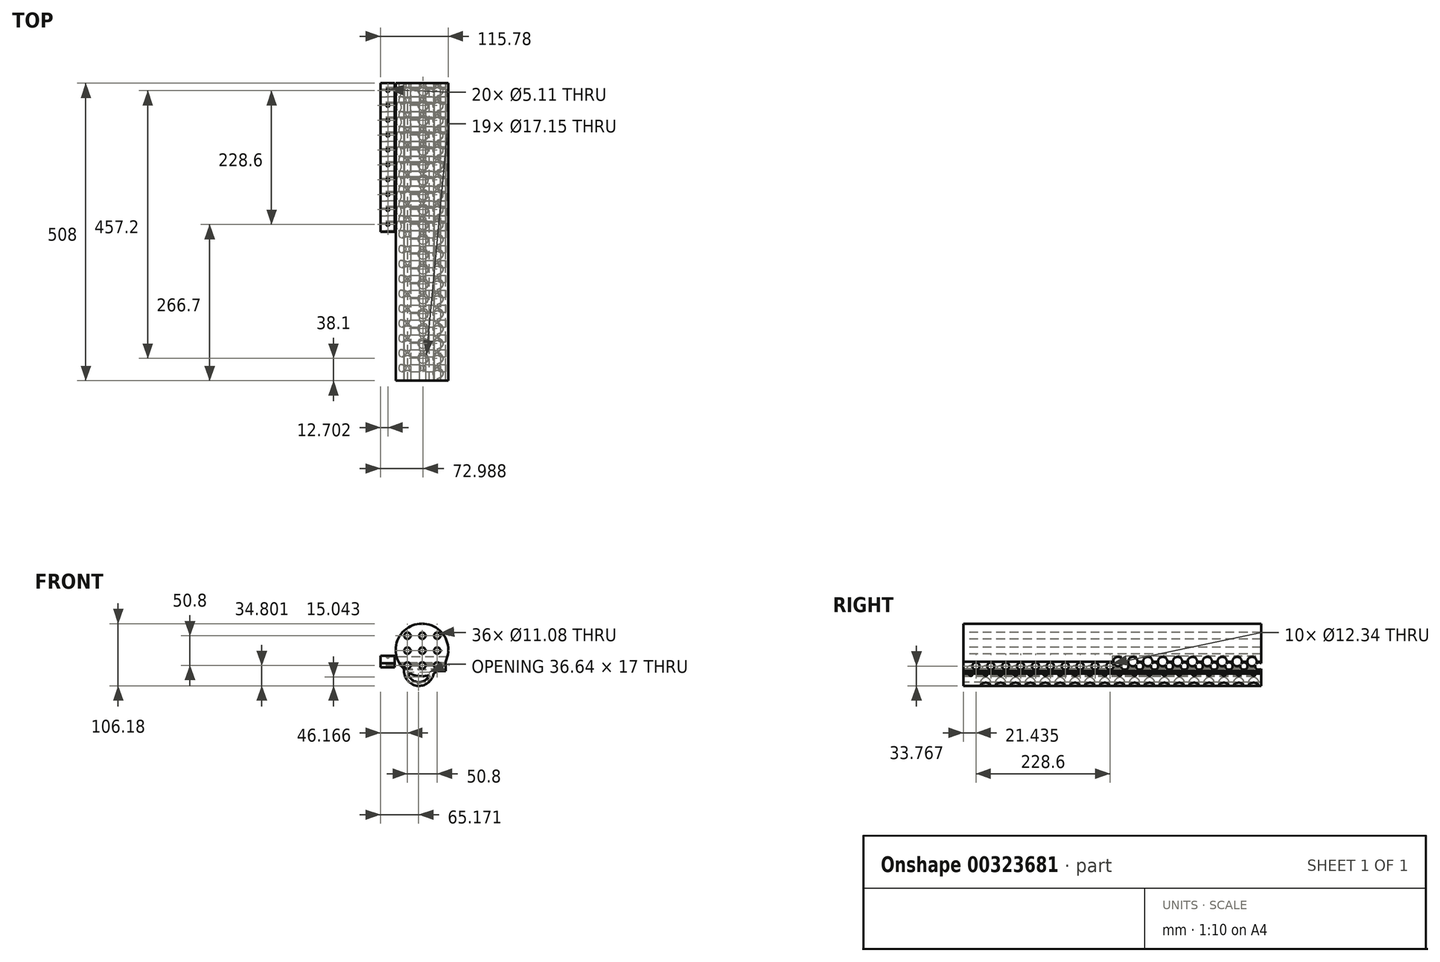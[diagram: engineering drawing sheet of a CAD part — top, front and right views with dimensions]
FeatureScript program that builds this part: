
annotation { "Feature Type Name" : "Feature", "Feature Type Description" : "" }
export const myFeature = defineFeature(function(context is Context, id is Id, definition is map)
    precondition{}
    {
        {
            var Q0;
            Q0=qCreatedBy(makeId("Front.planeOp"),FACE);
            var sketch = newSketch(context, id + "F0", { "sketchPlane" : qUnion([Q0])});
            skCircle(sketch, "E0", {"center": v(0, 0) * mm, "radius": 25.4 * mm});
            skSolve(sketch);
        }
        {
            var Q0;
            Q0=makeQuery(id+"F0.imprint","IMPRINT",FACE,{"disambiguationData":[TD([[makeQuery(id+"F0.imprint","IMPRINT",EDGE,{"derivedFrom":sQuery(id+"F0.wireOp",EDGE,"E0")}),1.0]])]});
            extrude(context, id + "F1", {"entities" : qUnion([Q0]), "depth" : 508 * mm});
        }
        {
            var Q0;
            Q0=makeQuery(id+"F1.opExtrude","CAP_FACE",FACE,{"disambiguationData":[OSD([sQuery(id+"F0.wireOp",EDGE,"E0")])],"isStart":false});
            var sketch = newSketch(context, id + "F2", { "sketchPlane" : qUnion([Q0])});
            skCircle(sketch, "E1", {"center": v(0, 0) * mm, "radius": 19.05 * mm});
            skSolve(sketch);
        }
        {
            var Q0;
            Q0=makeQuery(id+"F2.imprint","IMPRINT",FACE,{"disambiguationData":[TD([[makeQuery(id+"F2.imprint","IMPRINT",EDGE,{"derivedFrom":sQuery(id+"F2.wireOp",EDGE,"E1")}),1.0]])]});
            extrude(context, id + "F3", {"entities" : qUnion([Q0]), "operationType" : NewBodyOperationType.REMOVE, "oppositeDirection" : true, "depth" : 508 * mm});
        }
        {
            var Q0;
            Q0=qCreatedBy(makeId("Front.planeOp"),FACE);
            var sketch = newSketch(context, id + "F4", { "sketchPlane" : qUnion([Q0])});
            skLineSegment(sketch, "E2.bottom", {"start": v(-65.8, 26.01) * mm, "end": v(-41.62, 26.01) * mm});
            skLineSegment(sketch, "E2.top", {"start": v(-65.8, 6.33) * mm, "end": v(-41.62, 6.33) * mm});
            skLineSegment(sketch, "E2.left", {"start": v(-65.8, 26.01) * mm, "end": v(-65.8, 6.33) * mm});
            skLineSegment(sketch, "E2.right", {"start": v(-41.62, 26.01) * mm, "end": v(-41.62, 6.33) * mm});
            skSolve(sketch);
        }
        {
            var Q0;
            Q0=makeQuery(id+"F4.imprint","IMPRINT",FACE,{"disambiguationData":[TD([[makeQuery(id+"F4.imprint","IMPRINT",EDGE,{"derivedFrom":sQuery(id+"F4.wireOp",EDGE,"E2.bottom")}),-1.0]])]});
            extrude(context, id + "F5", {"entities" : qUnion([Q0]), "depth" : 254 * mm});
        }
        {
            var Q0;
            Q0=makeQuery(id+"F5.opExtrude","SWEPT_FACE",FACE,{"disambiguationData":[OSD([sQuery(id+"F4.wireOp",EDGE,"E2.top")])]});
            var sketch = newSketch(context, id + "F6", { "sketchPlane" : qUnion([Q0])});
            skCircle(sketch, "E3", {"center": v(-53.1, 241.3) * mm, "radius": 2.55 * mm});
            skCircle(sketch, "E4.0.1.0", {"center": v(-53.1, 215.9) * mm, "radius": 2.55 * mm});
            skCircle(sketch, "E4.0.2.0", {"center": v(-53.1, 190.5) * mm, "radius": 2.55 * mm});
            skCircle(sketch, "E4.0.3.0", {"center": v(-53.1, 165.1) * mm, "radius": 2.55 * mm});
            skCircle(sketch, "E4.0.4.0", {"center": v(-53.1, 139.7) * mm, "radius": 2.55 * mm});
            skCircle(sketch, "E4.0.5.0", {"center": v(-53.1, 114.3) * mm, "radius": 2.55 * mm});
            skCircle(sketch, "E4.0.6.0", {"center": v(-53.1, 88.9) * mm, "radius": 2.55 * mm});
            skCircle(sketch, "E4.0.7.0", {"center": v(-53.1, 63.5) * mm, "radius": 2.55 * mm});
            skCircle(sketch, "E4.0.8.0", {"center": v(-53.1, 38.1) * mm, "radius": 2.55 * mm});
            skCircle(sketch, "E4.0.9.0", {"center": v(-53.1, 12.7) * mm, "radius": 2.55 * mm});
            skLineSegment(sketch, "E4.direction1", {"start": v(-53.1, 241.3) * mm, "end": v(-27.7, 241.3) * mm, "construction": true});
            skLineSegment(sketch, "E4.direction2", {"start": v(-53.1, 241.3) * mm, "end": v(-53.1, 215.9) * mm, "construction": true});
            skSolve(sketch);
        }
        {
            var Q0;
            Q0 = qSketchRegion(id + "F6", true);
            extrude(context, id + "F7", {"entities" : qUnion([Q0]), "operationType" : NewBodyOperationType.REMOVE, "oppositeDirection" : true, "depth" : 254 * mm});
        }
        {
            var Q0;
            Q0=qCreatedBy(makeId("Front.planeOp"),FACE);
            var sketch = newSketch(context, id + "F8", { "sketchPlane" : qUnion([Q0])});
            skLineSegment(sketch, "E5.bottom", {"start": v(-16.31, 30.8) * mm, "end": v(45.28, 30.8) * mm});
            skLineSegment(sketch, "E5.top", {"start": v(-16.31, 0) * mm, "end": v(45.28, 0) * mm});
            skLineSegment(sketch, "E5.left", {"start": v(-16.31, 30.8) * mm, "end": v(-16.31, 0) * mm});
            skLineSegment(sketch, "E5.right", {"start": v(45.28, 30.8) * mm, "end": v(45.28, 0) * mm});
            skSolve(sketch);
        }
        {
            var Q0;
            Q0=makeQuery(id+"F8.imprint","IMPRINT",FACE,{"disambiguationData":[TD([[makeQuery(id+"F8.imprint","IMPRINT",EDGE,{"derivedFrom":sQuery(id+"F8.wireOp",EDGE,"E5.bottom")}),-1.0]])]});
            extrude(context, id + "F9", {"entities" : qUnion([Q0]), "operationType" : NewBodyOperationType.ADD, "depth" : 508 * mm});
        }
        {
            var Q0;
            Q0=makeQuery(id+"F9.opExtrude","SWEPT_FACE",FACE,{"disambiguationData":[OSD([sQuery(id+"F8.wireOp",EDGE,"E5.bottom")])]});
            var sketch = newSketch(context, id + "F10", { "sketchPlane" : qUnion([Q0])});
            skCircle(sketch, "E6", {"center": v(32.58, -495.3) * mm, "radius": 8.58 * mm});
            skCircle(sketch, "E7.0.1.0", {"center": v(32.58, -469.9) * mm, "radius": 8.58 * mm});
            skCircle(sketch, "E7.0.2.0", {"center": v(32.58, -444.5) * mm, "radius": 8.58 * mm});
            skCircle(sketch, "E7.0.3.0", {"center": v(32.58, -419.1) * mm, "radius": 8.58 * mm});
            skCircle(sketch, "E7.0.4.0", {"center": v(32.58, -393.7) * mm, "radius": 8.58 * mm});
            skCircle(sketch, "E7.0.5.0", {"center": v(32.58, -368.3) * mm, "radius": 8.58 * mm});
            skCircle(sketch, "E7.0.6.0", {"center": v(32.58, -342.9) * mm, "radius": 8.58 * mm});
            skCircle(sketch, "E7.0.7.0", {"center": v(32.58, -317.5) * mm, "radius": 8.58 * mm});
            skCircle(sketch, "E7.0.8.0", {"center": v(32.58, -292.1) * mm, "radius": 8.58 * mm});
            skCircle(sketch, "E7.0.9.0", {"center": v(32.58, -266.7) * mm, "radius": 8.58 * mm});
            skCircle(sketch, "E7.0.10.0", {"center": v(32.58, -241.3) * mm, "radius": 8.58 * mm});
            skCircle(sketch, "E7.0.11.0", {"center": v(32.58, -215.9) * mm, "radius": 8.58 * mm});
            skCircle(sketch, "E7.0.12.0", {"center": v(32.58, -190.5) * mm, "radius": 8.58 * mm});
            skCircle(sketch, "E7.0.13.0", {"center": v(32.58, -165.1) * mm, "radius": 8.58 * mm});
            skCircle(sketch, "E7.0.14.0", {"center": v(32.58, -139.7) * mm, "radius": 8.58 * mm});
            skCircle(sketch, "E7.0.15.0", {"center": v(32.58, -114.3) * mm, "radius": 8.58 * mm});
            skCircle(sketch, "E7.0.16.0", {"center": v(32.58, -88.9) * mm, "radius": 8.58 * mm});
            skCircle(sketch, "E7.0.17.0", {"center": v(32.58, -63.5) * mm, "radius": 8.58 * mm});
            skCircle(sketch, "E7.0.18.0", {"center": v(32.58, -38.1) * mm, "radius": 8.58 * mm});
            skCircle(sketch, "E7.0.19.0", {"center": v(32.58, -12.7) * mm, "radius": 8.58 * mm});
            skCircle(sketch, "E7.1.0.0", {"center": v(7.18, -495.3) * mm, "radius": 8.58 * mm});
            skCircle(sketch, "E7.1.1.0", {"center": v(7.18, -469.9) * mm, "radius": 8.58 * mm});
            skCircle(sketch, "E7.1.2.0", {"center": v(7.18, -444.5) * mm, "radius": 8.58 * mm});
            skCircle(sketch, "E7.1.3.0", {"center": v(7.18, -419.1) * mm, "radius": 8.58 * mm});
            skCircle(sketch, "E7.1.4.0", {"center": v(7.18, -393.7) * mm, "radius": 8.58 * mm});
            skCircle(sketch, "E7.1.5.0", {"center": v(7.18, -368.3) * mm, "radius": 8.58 * mm});
            skCircle(sketch, "E7.1.6.0", {"center": v(7.18, -342.9) * mm, "radius": 8.58 * mm});
            skCircle(sketch, "E7.1.7.0", {"center": v(7.18, -317.5) * mm, "radius": 8.58 * mm});
            skCircle(sketch, "E7.1.8.0", {"center": v(7.18, -292.1) * mm, "radius": 8.58 * mm});
            skCircle(sketch, "E7.1.9.0", {"center": v(7.18, -266.7) * mm, "radius": 8.58 * mm});
            skCircle(sketch, "E7.1.10.0", {"center": v(7.18, -241.3) * mm, "radius": 8.58 * mm});
            skCircle(sketch, "E7.1.11.0", {"center": v(7.18, -215.9) * mm, "radius": 8.58 * mm});
            skCircle(sketch, "E7.1.12.0", {"center": v(7.18, -190.5) * mm, "radius": 8.58 * mm});
            skCircle(sketch, "E7.1.13.0", {"center": v(7.18, -165.1) * mm, "radius": 8.58 * mm});
            skCircle(sketch, "E7.1.14.0", {"center": v(7.18, -139.7) * mm, "radius": 8.58 * mm});
            skCircle(sketch, "E7.1.15.0", {"center": v(7.18, -114.3) * mm, "radius": 8.58 * mm});
            skCircle(sketch, "E7.1.16.0", {"center": v(7.18, -88.9) * mm, "radius": 8.58 * mm});
            skCircle(sketch, "E7.1.17.0", {"center": v(7.18, -63.5) * mm, "radius": 8.58 * mm});
            skCircle(sketch, "E7.1.18.0", {"center": v(7.18, -38.1) * mm, "radius": 8.58 * mm});
            skCircle(sketch, "E7.1.19.0", {"center": v(7.18, -12.7) * mm, "radius": 8.58 * mm});
            skLineSegment(sketch, "E7.direction1", {"start": v(32.58, -495.3) * mm, "end": v(7.18, -495.3) * mm, "construction": true});
            skLineSegment(sketch, "E7.direction2", {"start": v(32.58, -495.3) * mm, "end": v(32.58, -469.9) * mm, "construction": true});
            skSolve(sketch);
        }
        {
            var Q0;
            Q0=makeQuery(id+"F10.imprint","IMPRINT",FACE,{"disambiguationData":[TD([[makeQuery(id+"F10.imprint","IMPRINT",EDGE,{"derivedFrom":sQuery(id+"F10.wireOp",EDGE,"E6")}),1.0]])]});
            var Q1;
            Q1=makeQuery(id+"F10.imprint","IMPRINT",FACE,{"disambiguationData":[TD([[makeQuery(id+"F10.imprint","IMPRINT",EDGE,{"derivedFrom":sQuery(id+"F10.wireOp",EDGE,"E7.0.1.0")}),1.0]])]});
            var Q2;
            Q2=makeQuery(id+"F10.imprint","IMPRINT",FACE,{"disambiguationData":[TD([[makeQuery(id+"F10.imprint","IMPRINT",EDGE,{"derivedFrom":sQuery(id+"F10.wireOp",EDGE,"E7.0.2.0")}),1.0]])]});
            var Q3;
            Q3=makeQuery(id+"F10.imprint","IMPRINT",FACE,{"disambiguationData":[TD([[makeQuery(id+"F10.imprint","IMPRINT",EDGE,{"derivedFrom":sQuery(id+"F10.wireOp",EDGE,"E7.0.3.0")}),1.0]])]});
            var Q4;
            Q4=makeQuery(id+"F10.imprint","IMPRINT",FACE,{"disambiguationData":[TD([[makeQuery(id+"F10.imprint","IMPRINT",EDGE,{"derivedFrom":sQuery(id+"F10.wireOp",EDGE,"E7.0.4.0")}),1.0]])]});
            var Q5;
            Q5=makeQuery(id+"F10.imprint","IMPRINT",FACE,{"disambiguationData":[TD([[makeQuery(id+"F10.imprint","IMPRINT",EDGE,{"derivedFrom":sQuery(id+"F10.wireOp",EDGE,"E7.0.5.0")}),1.0]])]});
            var Q6;
            Q6=makeQuery(id+"F10.imprint","IMPRINT",FACE,{"disambiguationData":[TD([[makeQuery(id+"F10.imprint","IMPRINT",EDGE,{"derivedFrom":sQuery(id+"F10.wireOp",EDGE,"E7.0.6.0")}),1.0]])]});
            var Q7;
            Q7=makeQuery(id+"F10.imprint","IMPRINT",FACE,{"disambiguationData":[TD([[makeQuery(id+"F10.imprint","IMPRINT",EDGE,{"derivedFrom":sQuery(id+"F10.wireOp",EDGE,"E7.0.7.0")}),1.0]])]});
            var Q8;
            Q8=makeQuery(id+"F10.imprint","IMPRINT",FACE,{"disambiguationData":[TD([[makeQuery(id+"F10.imprint","IMPRINT",EDGE,{"derivedFrom":sQuery(id+"F10.wireOp",EDGE,"E7.0.8.0")}),1.0]])]});
            var Q9;
            Q9=makeQuery(id+"F10.imprint","IMPRINT",FACE,{"disambiguationData":[TD([[makeQuery(id+"F10.imprint","IMPRINT",EDGE,{"derivedFrom":sQuery(id+"F10.wireOp",EDGE,"E7.0.9.0")}),1.0]])]});
            var Q10;
            Q10=makeQuery(id+"F10.imprint","IMPRINT",FACE,{"disambiguationData":[TD([[makeQuery(id+"F10.imprint","IMPRINT",EDGE,{"derivedFrom":sQuery(id+"F10.wireOp",EDGE,"E7.0.10.0")}),1.0]])]});
            var Q11;
            Q11=makeQuery(id+"F10.imprint","IMPRINT",FACE,{"disambiguationData":[TD([[makeQuery(id+"F10.imprint","IMPRINT",EDGE,{"derivedFrom":sQuery(id+"F10.wireOp",EDGE,"E7.0.11.0")}),1.0]])]});
            var Q12;
            Q12=makeQuery(id+"F10.imprint","IMPRINT",FACE,{"disambiguationData":[TD([[makeQuery(id+"F10.imprint","IMPRINT",EDGE,{"derivedFrom":sQuery(id+"F10.wireOp",EDGE,"E7.0.12.0")}),1.0]])]});
            var Q13;
            Q13=makeQuery(id+"F10.imprint","IMPRINT",FACE,{"disambiguationData":[TD([[makeQuery(id+"F10.imprint","IMPRINT",EDGE,{"derivedFrom":sQuery(id+"F10.wireOp",EDGE,"E7.0.13.0")}),1.0]])]});
            var Q14;
            Q14=makeQuery(id+"F10.imprint","IMPRINT",FACE,{"disambiguationData":[TD([[makeQuery(id+"F10.imprint","IMPRINT",EDGE,{"derivedFrom":sQuery(id+"F10.wireOp",EDGE,"E7.0.14.0")}),1.0]])]});
            var Q15;
            Q15=makeQuery(id+"F10.imprint","IMPRINT",FACE,{"disambiguationData":[TD([[makeQuery(id+"F10.imprint","IMPRINT",EDGE,{"derivedFrom":sQuery(id+"F10.wireOp",EDGE,"E7.0.15.0")}),1.0]])]});
            var Q16;
            Q16=makeQuery(id+"F10.imprint","IMPRINT",FACE,{"disambiguationData":[TD([[makeQuery(id+"F10.imprint","IMPRINT",EDGE,{"derivedFrom":sQuery(id+"F10.wireOp",EDGE,"E7.0.16.0")}),1.0]])]});
            var Q17;
            Q17=makeQuery(id+"F10.imprint","IMPRINT",FACE,{"disambiguationData":[TD([[makeQuery(id+"F10.imprint","IMPRINT",EDGE,{"derivedFrom":sQuery(id+"F10.wireOp",EDGE,"E7.0.17.0")}),1.0]])]});
            var Q18;
            Q18=makeQuery(id+"F10.imprint","IMPRINT",FACE,{"disambiguationData":[TD([[makeQuery(id+"F10.imprint","IMPRINT",EDGE,{"derivedFrom":sQuery(id+"F10.wireOp",EDGE,"E7.0.18.0")}),1.0]])]});
            var Q19;
            Q19=makeQuery(id+"F10.imprint","IMPRINT",FACE,{"disambiguationData":[TD([[makeQuery(id+"F10.imprint","IMPRINT",EDGE,{"derivedFrom":sQuery(id+"F10.wireOp",EDGE,"E7.0.19.0")}),1.0]])]});
            var Q20;
            Q20=makeQuery(id+"F10.imprint","IMPRINT",FACE,{"disambiguationData":[TD([[makeQuery(id+"F10.imprint","IMPRINT",EDGE,{"derivedFrom":sQuery(id+"F10.wireOp",EDGE,"E7.1.1.0")}),1.0]])]});
            var Q21;
            Q21=makeQuery(id+"F10.imprint","IMPRINT",FACE,{"disambiguationData":[TD([[makeQuery(id+"F10.imprint","IMPRINT",EDGE,{"derivedFrom":sQuery(id+"F10.wireOp",EDGE,"E7.1.2.0")}),1.0]])]});
            var Q22;
            Q22=makeQuery(id+"F10.imprint","IMPRINT",FACE,{"disambiguationData":[TD([[makeQuery(id+"F10.imprint","IMPRINT",EDGE,{"derivedFrom":sQuery(id+"F10.wireOp",EDGE,"E7.1.3.0")}),1.0]])]});
            var Q23;
            Q23=makeQuery(id+"F10.imprint","IMPRINT",FACE,{"disambiguationData":[TD([[makeQuery(id+"F10.imprint","IMPRINT",EDGE,{"derivedFrom":sQuery(id+"F10.wireOp",EDGE,"E7.1.4.0")}),1.0]])]});
            var Q24;
            Q24=makeQuery(id+"F10.imprint","IMPRINT",FACE,{"disambiguationData":[TD([[makeQuery(id+"F10.imprint","IMPRINT",EDGE,{"derivedFrom":sQuery(id+"F10.wireOp",EDGE,"E7.1.5.0")}),1.0]])]});
            var Q25;
            Q25=makeQuery(id+"F10.imprint","IMPRINT",FACE,{"disambiguationData":[TD([[makeQuery(id+"F10.imprint","IMPRINT",EDGE,{"derivedFrom":sQuery(id+"F10.wireOp",EDGE,"E7.1.6.0")}),1.0]])]});
            var Q26;
            Q26=makeQuery(id+"F10.imprint","IMPRINT",FACE,{"disambiguationData":[TD([[makeQuery(id+"F10.imprint","IMPRINT",EDGE,{"derivedFrom":sQuery(id+"F10.wireOp",EDGE,"E7.1.7.0")}),1.0]])]});
            var Q27;
            Q27=makeQuery(id+"F10.imprint","IMPRINT",FACE,{"disambiguationData":[TD([[makeQuery(id+"F10.imprint","IMPRINT",EDGE,{"derivedFrom":sQuery(id+"F10.wireOp",EDGE,"E7.1.8.0")}),1.0]])]});
            var Q28;
            Q28=makeQuery(id+"F10.imprint","IMPRINT",FACE,{"disambiguationData":[TD([[makeQuery(id+"F10.imprint","IMPRINT",EDGE,{"derivedFrom":sQuery(id+"F10.wireOp",EDGE,"E7.1.9.0")}),1.0]])]});
            var Q29;
            Q29=makeQuery(id+"F10.imprint","IMPRINT",FACE,{"disambiguationData":[TD([[makeQuery(id+"F10.imprint","IMPRINT",EDGE,{"derivedFrom":sQuery(id+"F10.wireOp",EDGE,"E7.1.10.0")}),1.0]])]});
            var Q30;
            Q30=makeQuery(id+"F10.imprint","IMPRINT",FACE,{"disambiguationData":[TD([[makeQuery(id+"F10.imprint","IMPRINT",EDGE,{"derivedFrom":sQuery(id+"F10.wireOp",EDGE,"E7.1.11.0")}),1.0]])]});
            var Q31;
            Q31=makeQuery(id+"F10.imprint","IMPRINT",FACE,{"disambiguationData":[TD([[makeQuery(id+"F10.imprint","IMPRINT",EDGE,{"derivedFrom":sQuery(id+"F10.wireOp",EDGE,"E7.1.12.0")}),1.0]])]});
            var Q32;
            Q32=makeQuery(id+"F10.imprint","IMPRINT",FACE,{"disambiguationData":[TD([[makeQuery(id+"F10.imprint","IMPRINT",EDGE,{"derivedFrom":sQuery(id+"F10.wireOp",EDGE,"E7.1.13.0")}),1.0]])]});
            var Q33;
            Q33=makeQuery(id+"F10.imprint","IMPRINT",FACE,{"disambiguationData":[TD([[makeQuery(id+"F10.imprint","IMPRINT",EDGE,{"derivedFrom":sQuery(id+"F10.wireOp",EDGE,"E7.1.14.0")}),1.0]])]});
            var Q34;
            Q34=makeQuery(id+"F10.imprint","IMPRINT",FACE,{"disambiguationData":[TD([[makeQuery(id+"F10.imprint","IMPRINT",EDGE,{"derivedFrom":sQuery(id+"F10.wireOp",EDGE,"E7.1.15.0")}),1.0]])]});
            var Q35;
            Q35=makeQuery(id+"F10.imprint","IMPRINT",FACE,{"disambiguationData":[TD([[makeQuery(id+"F10.imprint","IMPRINT",EDGE,{"derivedFrom":sQuery(id+"F10.wireOp",EDGE,"E7.1.16.0")}),1.0]])]});
            var Q36;
            Q36=makeQuery(id+"F10.imprint","IMPRINT",FACE,{"disambiguationData":[TD([[makeQuery(id+"F10.imprint","IMPRINT",EDGE,{"derivedFrom":sQuery(id+"F10.wireOp",EDGE,"E7.1.17.0")}),1.0]])]});
            var Q37;
            Q37=makeQuery(id+"F10.imprint","IMPRINT",FACE,{"disambiguationData":[TD([[makeQuery(id+"F10.imprint","IMPRINT",EDGE,{"derivedFrom":sQuery(id+"F10.wireOp",EDGE,"E7.1.18.0")}),1.0]])]});
            var Q38;
            Q38=makeQuery(id+"F10.imprint","IMPRINT",FACE,{"disambiguationData":[TD([[makeQuery(id+"F10.imprint","IMPRINT",EDGE,{"derivedFrom":sQuery(id+"F10.wireOp",EDGE,"E7.1.19.0")}),1.0]])]});
            extrude(context, id + "F11", {"entities" : qUnion([Q0, Q1, Q2, Q3, Q4, Q5, Q6, Q7, Q8, Q9, Q10, Q11, Q12, Q13, Q14, Q15, Q16, Q17, Q18, Q19, Q20, Q21, Q22, Q23, Q24, Q25, Q26, Q27, Q28, Q29, Q30, Q31, Q32, Q33, Q34, Q35, Q36, Q37, Q38]), "operationType" : NewBodyOperationType.REMOVE, "oppositeDirection" : true, "depth" : 508 * mm});
        }
        {
            var Q0;
            Q0=qCreatedBy(makeId("Front.planeOp"),FACE);
            var sketch = newSketch(context, id + "F12", { "sketchPlane" : qUnion([Q0])});
            skCircle(sketch, "E8", {"center": v(5.14, 35.95) * mm, "radius": 44.83 * mm});
            skSolve(sketch);
        }
        {
            var Q0;
            Q0=makeQuery(id+"F12.imprint","IMPRINT",FACE,{"disambiguationData":[TD([[makeQuery(id+"F12.imprint","IMPRINT",EDGE,{"derivedFrom":sQuery(id+"F12.wireOp",EDGE,"E8")}),1.0]])]});
            extrude(context, id + "F13", {"entities" : qUnion([Q0]), "operationType" : NewBodyOperationType.ADD, "depth" : 508 * mm});
        }
        {
            var Q0;
            Q0=makeQuery(id+"F13.boolean.opBoolean","MERGE",FACE,{"derivedFrom":[makeQuery(id+"F9.boolean.opBoolean","MERGE",FACE,{"derivedFrom":[makeQuery(id+"F1.opExtrude","CAP_FACE",FACE,{"disambiguationData":[OSD([sQuery(id+"F0.wireOp",EDGE,"E0")])],"isStart":false}),makeQuery(id+"F9.opExtrude","CAP_FACE",FACE,{"disambiguationData":[OSD([sQuery(id+"F8.wireOp",EDGE,"E5.bottom"),sQuery(id+"F8.wireOp",EDGE,"E5.top"),sQuery(id+"F8.wireOp",EDGE,"E5.left"),sQuery(id+"F8.wireOp",EDGE,"E5.right")])],"isStart":false})]}),makeQuery(id+"F13.opExtrude","CAP_FACE",FACE,{"disambiguationData":[OSD([sQuery(id+"F12.wireOp",EDGE,"E8")])],"isStart":false})]});
            var sketch = newSketch(context, id + "F14", { "sketchPlane" : qUnion([Q0])});
            skCircle(sketch, "E9", {"center": v(-19.64, 60.2) * mm, "radius": 5.54 * mm});
            skCircle(sketch, "E10.0.1.0", {"center": v(-19.64, 34.8) * mm, "radius": 5.54 * mm});
            skCircle(sketch, "E10.0.2.0", {"center": v(-19.64, 9.4) * mm, "radius": 5.54 * mm});
            skCircle(sketch, "E10.1.0.0", {"center": v(5.76, 60.2) * mm, "radius": 5.54 * mm});
            skCircle(sketch, "E10.1.1.0", {"center": v(5.76, 34.8) * mm, "radius": 5.54 * mm});
            skCircle(sketch, "E10.1.2.0", {"center": v(5.76, 9.4) * mm, "radius": 5.54 * mm});
            skCircle(sketch, "E10.2.0.0", {"center": v(31.16, 60.2) * mm, "radius": 5.54 * mm});
            skCircle(sketch, "E10.2.1.0", {"center": v(31.16, 34.8) * mm, "radius": 5.54 * mm});
            skCircle(sketch, "E10.2.2.0", {"center": v(31.16, 9.4) * mm, "radius": 5.54 * mm});
            skLineSegment(sketch, "E10.direction1", {"start": v(-19.64, 60.2) * mm, "end": v(5.76, 60.2) * mm, "construction": true});
            skLineSegment(sketch, "E10.direction2", {"start": v(-19.64, 60.2) * mm, "end": v(-19.64, 34.8) * mm, "construction": true});
            skSolve(sketch);
        }
        {
            var Q0;
            Q0 = qSketchRegion(id + "F14", true);
            extrude(context, id + "F15", {"entities" : qUnion([Q0]), "operationType" : NewBodyOperationType.REMOVE, "oppositeDirection" : true, "depth" : 762 * mm});
        }
        {
            var Q0;
            Q0=makeQuery(id+"F9.opExtrude","SWEPT_FACE",FACE,{"disambiguationData":[OSD([sQuery(id+"F8.wireOp",EDGE,"E5.right")])]});
            var sketch = newSketch(context, id + "F16", { "sketchPlane" : qUnion([Q0])});
            skCircle(sketch, "E11", {"center": v(-486.57, 8.37) * mm, "radius": 6.17 * mm});
            skCircle(sketch, "E12.1.0.0", {"center": v(-461.17, 8.37) * mm, "radius": 6.17 * mm});
            skCircle(sketch, "E12.2.0.0", {"center": v(-435.77, 8.37) * mm, "radius": 6.17 * mm});
            skCircle(sketch, "E12.3.0.0", {"center": v(-410.37, 8.37) * mm, "radius": 6.17 * mm});
            skCircle(sketch, "E12.4.0.0", {"center": v(-384.97, 8.37) * mm, "radius": 6.17 * mm});
            skCircle(sketch, "E12.5.0.0", {"center": v(-359.57, 8.37) * mm, "radius": 6.17 * mm});
            skCircle(sketch, "E12.6.0.0", {"center": v(-334.17, 8.37) * mm, "radius": 6.17 * mm});
            skCircle(sketch, "E12.7.0.0", {"center": v(-308.77, 8.37) * mm, "radius": 6.17 * mm});
            skCircle(sketch, "E12.8.0.0", {"center": v(-283.37, 8.37) * mm, "radius": 6.17 * mm});
            skCircle(sketch, "E12.9.0.0", {"center": v(-257.97, 8.37) * mm, "radius": 6.17 * mm});
            skCircle(sketch, "E12.10.0.0", {"center": v(-232.57, 8.37) * mm, "radius": 6.17 * mm});
            skCircle(sketch, "E12.11.0.0", {"center": v(-207.17, 8.37) * mm, "radius": 6.17 * mm});
            skCircle(sketch, "E12.12.0.0", {"center": v(-181.77, 8.37) * mm, "radius": 6.17 * mm});
            skCircle(sketch, "E12.13.0.0", {"center": v(-156.37, 8.37) * mm, "radius": 6.17 * mm});
            skCircle(sketch, "E12.14.0.0", {"center": v(-130.97, 8.37) * mm, "radius": 6.17 * mm});
            skCircle(sketch, "E12.15.0.0", {"center": v(-105.57, 8.37) * mm, "radius": 6.17 * mm});
            skCircle(sketch, "E12.16.0.0", {"center": v(-80.17, 8.37) * mm, "radius": 6.17 * mm});
            skCircle(sketch, "E12.17.0.0", {"center": v(-54.77, 8.37) * mm, "radius": 6.17 * mm});
            skCircle(sketch, "E12.18.0.0", {"center": v(-29.37, 8.37) * mm, "radius": 6.17 * mm});
            skCircle(sketch, "E12.19.0.0", {"center": v(-3.97, 8.37) * mm, "radius": 6.17 * mm});
            skLineSegment(sketch, "E12.direction1", {"start": v(-486.57, 8.37) * mm, "end": v(-461.17, 8.37) * mm, "construction": true});
            skSolve(sketch);
        }
        {
            var Q0;
            Q0 = qSketchRegion(id + "F16", true);
            extrude(context, id + "F17", {"entities" : qUnion([Q0]), "operationType" : NewBodyOperationType.REMOVE, "oppositeDirection" : true, "depth" : 508 * mm});
        }
        {
            var Q0;
            Q0=makeQuery(id+"F5.opExtrude","SWEPT_FACE",FACE,{"disambiguationData":[OSD([sQuery(id+"F4.wireOp",EDGE,"E2.left")])]});
            var sketch = newSketch(context, id + "F18", { "sketchPlane" : qUnion([Q0])});
            skCircle(sketch, "E13", {"center": v(244.14, 16.17) * mm, "radius": 8.06 * mm});
            skPoint(sketch, "E13.centerSnap0", {"position": v(254, 16.17) * mm});
            skCircle(sketch, "E14.1.0.0", {"center": v(218.74, 16.17) * mm, "radius": 8.06 * mm});
            skCircle(sketch, "E14.2.0.0", {"center": v(193.34, 16.17) * mm, "radius": 8.06 * mm});
            skCircle(sketch, "E14.3.0.0", {"center": v(167.94, 16.17) * mm, "radius": 8.06 * mm});
            skCircle(sketch, "E14.4.0.0", {"center": v(142.54, 16.17) * mm, "radius": 8.06 * mm});
            skCircle(sketch, "E14.5.0.0", {"center": v(117.14, 16.17) * mm, "radius": 8.06 * mm});
            skCircle(sketch, "E14.6.0.0", {"center": v(91.74, 16.17) * mm, "radius": 8.06 * mm});
            skCircle(sketch, "E14.7.0.0", {"center": v(66.34, 16.17) * mm, "radius": 8.06 * mm});
            skCircle(sketch, "E14.8.0.0", {"center": v(40.94, 16.17) * mm, "radius": 8.06 * mm});
            skCircle(sketch, "E14.9.0.0", {"center": v(15.54, 16.17) * mm, "radius": 8.06 * mm});
            skCircle(sketch, "E14.10.0.0", {"center": v(-9.86, 16.17) * mm, "radius": 8.06 * mm});
            skCircle(sketch, "E14.11.0.0", {"center": v(-35.26, 16.17) * mm, "radius": 8.06 * mm});
            skCircle(sketch, "E14.12.0.0", {"center": v(-60.66, 16.17) * mm, "radius": 8.06 * mm});
            skCircle(sketch, "E14.13.0.0", {"center": v(-86.06, 16.17) * mm, "radius": 8.06 * mm});
            skCircle(sketch, "E14.14.0.0", {"center": v(-111.46, 16.17) * mm, "radius": 8.06 * mm});
            skCircle(sketch, "E14.15.0.0", {"center": v(-136.86, 16.17) * mm, "radius": 8.06 * mm});
            skCircle(sketch, "E14.16.0.0", {"center": v(-162.26, 16.17) * mm, "radius": 8.06 * mm});
            skCircle(sketch, "E14.17.0.0", {"center": v(-187.66, 16.17) * mm, "radius": 8.06 * mm});
            skCircle(sketch, "E14.18.0.0", {"center": v(-213.06, 16.17) * mm, "radius": 8.06 * mm});
            skCircle(sketch, "E14.19.0.0", {"center": v(-238.46, 16.17) * mm, "radius": 8.06 * mm});
            skLineSegment(sketch, "E14.direction1", {"start": v(244.14, 16.17) * mm, "end": v(218.74, 16.17) * mm, "construction": true});
            skSolve(sketch);
        }
        {
            var Q0;
            Q0=sQuery(id+"F18.wireOp",EDGE,"E14.1.0.0");
            extrude(context, id + "F19", {"bodyType" : ToolBodyType.SURFACE, "surfaceEntities" : qUnion([Q0]), "depth" : 25.4 * mm});
        }
        {
            var Q0;
            Q0 = qSketchRegion(id + "F18", true);
            extrude(context, id + "F20", {"entities" : qUnion([Q0]), "operationType" : NewBodyOperationType.REMOVE, "oppositeDirection" : true, "depth" : 508 * mm});
        }
    });
